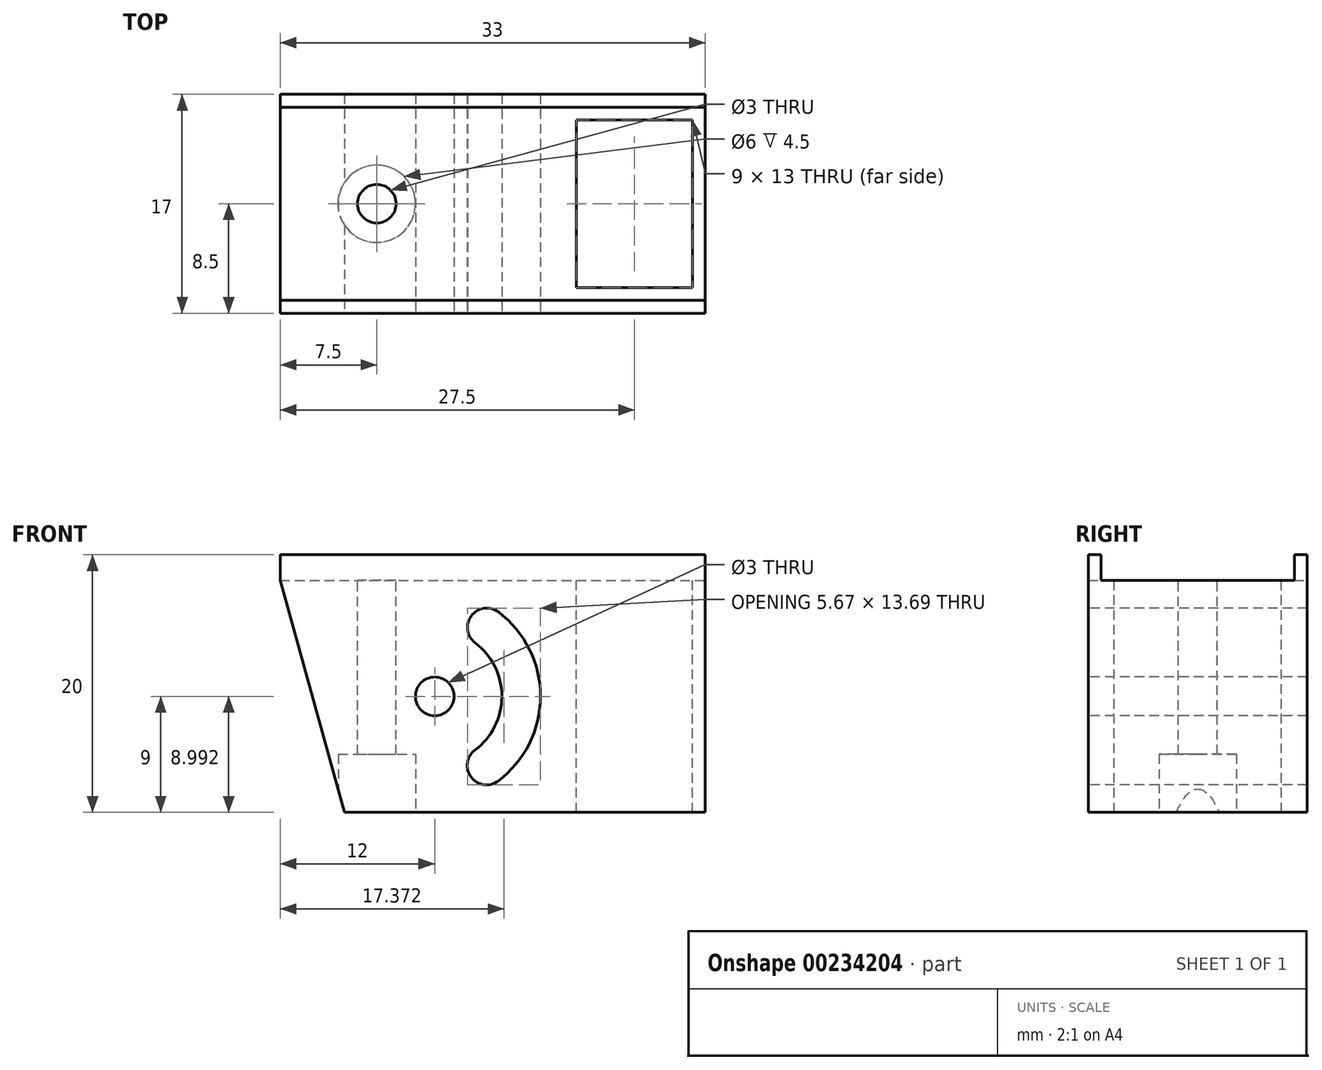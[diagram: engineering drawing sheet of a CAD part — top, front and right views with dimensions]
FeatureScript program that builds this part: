
annotation { "Feature Type Name" : "Feature", "Feature Type Description" : "" }
export const myFeature = defineFeature(function(context is Context, id is Id, definition is map)
    precondition{}
    {
        {
            var Q0;
            Q0=qCreatedBy(makeId("Top.planeOp"),FACE);
            var sketch = newSketch(context, id + "F0", { "sketchPlane" : qUnion([Q0])});
            skLineSegment(sketch, "E0.bottom", {"start": v(0, 0) * mm, "end": v(33, 0) * mm});
            skLineSegment(sketch, "E0.top", {"start": v(0, 17) * mm, "end": v(33, 17) * mm});
            skLineSegment(sketch, "E0.left", {"start": v(0, 0) * mm, "end": v(0, 17) * mm});
            skLineSegment(sketch, "E0.right", {"start": v(33, 0) * mm, "end": v(33, 17) * mm});
            skLineSegment(sketch, "E1.bottom", {"start": v(23, 2) * mm, "end": v(32, 2) * mm});
            skLineSegment(sketch, "E1.top", {"start": v(23, 15) * mm, "end": v(32, 15) * mm});
            skLineSegment(sketch, "E1.left", {"start": v(23, 2) * mm, "end": v(23, 15) * mm});
            skLineSegment(sketch, "E1.right", {"start": v(32, 2) * mm, "end": v(32, 15) * mm});
            skLineSegment(sketch, "E2", {"start": v(0, 8.5) * mm, "end": v(33, 8.5) * mm, "construction": true});
            skCircle(sketch, "E3", {"center": v(7.5, 8.5) * mm, "radius": 1.5 * mm});
            skLineSegment(sketch, "E4", {"start": v(0, 1) * mm, "end": v(33, 1) * mm});
            skLineSegment(sketch, "E5", {"start": v(0, 16) * mm, "end": v(33, 16) * mm});
            skSolve(sketch);
        }
        {
            var Q0;
            Q0=makeQuery(id+"F0.imprint","IMPRINT",FACE,{"disambiguationData":[TD([[makeQuery(id+"F0.imprint","IMPRINT",EDGE,{"derivedFrom":sQuery(id+"F0.wireOp",EDGE,"E0.bottom")}),1.0]])]});
            var Q1;
            Q1=makeQuery(id+"F0.imprint","IMPRINT",FACE,{"disambiguationData":[TD([[makeQuery(id+"F0.imprint","IMPRINT",EDGE,{"derivedFrom":sQuery(id+"F0.wireOp",EDGE,"E1.bottom")}),-1.0]])]});
            var Q2;
            {var subQ0=sQuery(id+"F0.wireOp",EDGE,"E0.top");Q2=makeQuery(id+"F0.imprint","IMPRINT",FACE,{"disambiguationData":[TD([[makeQuery(id+"F0.imprint","IMPRINT",EDGE,{"derivedFrom":subQ0}),-1.0]])]});}
            extrude(context, id + "F1", {"entities" : qUnion([Q0, Q1, Q2]), "oppositeDirection" : true, "depth" : 18 * mm});
        }
        {
            var Q0;
            Q0=makeQuery(id+"F1.opExtrude","SWEPT_FACE",FACE,{"disambiguationData":[OSD([sQuery(id+"F0.wireOp",EDGE,"E0.bottom")])]});
            var sketch = newSketch(context, id + "F2", { "sketchPlane" : qUnion([Q0])});
            skLineSegment(sketch, "E6", {"start": v(0, 0) * mm, "end": v(5, -18) * mm});
            skSolve(sketch);
        }
        {
            var Q0;
            Q0 = qSketchRegion(id + "F2", true);
            var Q1;
            {var subQ0=sQuery(id+"F2.wireOp",EDGE,"E6");Q1=makeQuery(id+"F2.imprint","IMPRINT",FACE,{"disambiguationData":[TD([[makeQuery(id+"F2.imprint","IMPRINT",EDGE,{"derivedFrom":subQ0}),-1.0]])]});}
            extrude(context, id + "F3", {"entities" : qUnion([Q0, Q1]), "operationType" : NewBodyOperationType.REMOVE, "endBound" : BoundingType.THROUGH_ALL, "oppositeDirection" : true, "depth" : 25 * mm});
        }
        {
            var Q0;
            Q0=makeQuery(id+"F1.opExtrude","SWEPT_FACE",FACE,{"disambiguationData":[OSD([sQuery(id+"F0.wireOp",EDGE,"E0.bottom")])]});
            var sketch = newSketch(context, id + "F4", { "sketchPlane" : qUnion([Q0])});
            skLineSegment(sketch, "E7", {"start": v(2.5, -9) * mm, "end": v(33, -9) * mm, "construction": true});
            skCircle(sketch, "E8", {"center": v(12, -9) * mm, "radius": 1.5 * mm});
            skArc(sketch, "E9", {"start": v(16.95, -2.45) * mm, "mid": v(14.85, -2.74) * mm, "end": v(15.14, -4.84) * mm});
            skArc(sketch, "E10", {"start": v(15.12, -13.17) * mm, "mid": v(14.82, -15.27) * mm, "end": v(16.92, -15.57) * mm});
            skArc(sketch, "E11", {"start": v(15.14, -4.84) * mm, "mid": v(17.2, -9.01) * mm, "end": v(15.12, -13.17) * mm});
            skArc(sketch, "E12", {"start": v(16.95, -2.45) * mm, "mid": v(20.2, -9.02) * mm, "end": v(16.92, -15.57) * mm});
            skSolve(sketch);
        }
        {
            var Q0;
            Q0 = qSketchRegion(id + "F4", true);
            extrude(context, id + "F5", {"entities" : qUnion([Q0]), "operationType" : NewBodyOperationType.REMOVE, "endBound" : BoundingType.THROUGH_ALL, "oppositeDirection" : true, "depth" : 25 * mm});
        }
        {
            var Q0;
            Q0=makeQuery(id+"F1.opExtrude","CAP_FACE",FACE,{"disambiguationData":[OSD([sQuery(id+"F0.wireOp",EDGE,"E0.bottom"),sQuery(id+"F0.wireOp",EDGE,"E0.top"),sQuery(id+"F0.wireOp",EDGE,"E0.left"),sQuery(id+"F0.wireOp",EDGE,"E0.right"),sQuery(id+"F0.wireOp",EDGE,"E1.bottom"),sQuery(id+"F0.wireOp",EDGE,"E1.top"),sQuery(id+"F0.wireOp",EDGE,"E1.left"),sQuery(id+"F0.wireOp",EDGE,"E1.right"),sQuery(id+"F0.wireOp",EDGE,"E3")])],"isStart":false});
            var sketch = newSketch(context, id + "F6", { "sketchPlane" : qUnion([Q0])});
            skCircle(sketch, "E13", {"center": v(7.5, -8.5) * mm, "radius": 3 * mm});
            skSolve(sketch);
        }
        {
            var Q0;
            Q0 = qSketchRegion(id + "F6", true);
            extrude(context, id + "F7", {"entities" : qUnion([Q0]), "operationType" : NewBodyOperationType.REMOVE, "oppositeDirection" : true, "depth" : 4.5 * mm});
        }
        {
            var Q0;
            {var subQ0=sQuery(id+"F0.wireOp",EDGE,"E0.top");Q0=makeQuery(id+"F0.imprint","IMPRINT",FACE,{"disambiguationData":[TD([[makeQuery(id+"F0.imprint","IMPRINT",EDGE,{"derivedFrom":subQ0}),-1.0]])]});}
            var Q1;
            {var subQ0=sQuery(id+"F0.wireOp",EDGE,"E0.bottom");Q1=makeQuery(id+"F0.imprint","IMPRINT",FACE,{"disambiguationData":[TD([[makeQuery(id+"F0.imprint","IMPRINT",EDGE,{"derivedFrom":subQ0}),1.0]])]});}
            extrude(context, id + "F8", {"entities" : qUnion([Q0, Q1]), "operationType" : NewBodyOperationType.ADD, "depth" : 1 * mm});
        }
        {
            var Q0;
            Q0=makeQuery(id+"F8.opExtrude","CAP_FACE",FACE,{"disambiguationData":[OSD([sQuery(id+"F0.wireOp",EDGE,"E0.top"),sQuery(id+"F0.wireOp",EDGE,"E0.left"),sQuery(id+"F0.wireOp",EDGE,"E0.right"),sQuery(id+"F0.wireOp",EDGE,"E5")])],"isStart":false});
            var Q1;
            Q1=makeQuery(id+"F8.opExtrude","CAP_FACE",FACE,{"disambiguationData":[OSD([sQuery(id+"F0.wireOp",EDGE,"E0.bottom"),sQuery(id+"F0.wireOp",EDGE,"E0.left"),sQuery(id+"F0.wireOp",EDGE,"E0.right"),sQuery(id+"F0.wireOp",EDGE,"E4")])],"isStart":false});
            extrude(context, id + "F9", {"entities" : qUnion([Q0, Q1]), "operationType" : NewBodyOperationType.ADD, "depth" : 1 * mm});
        }
    });
